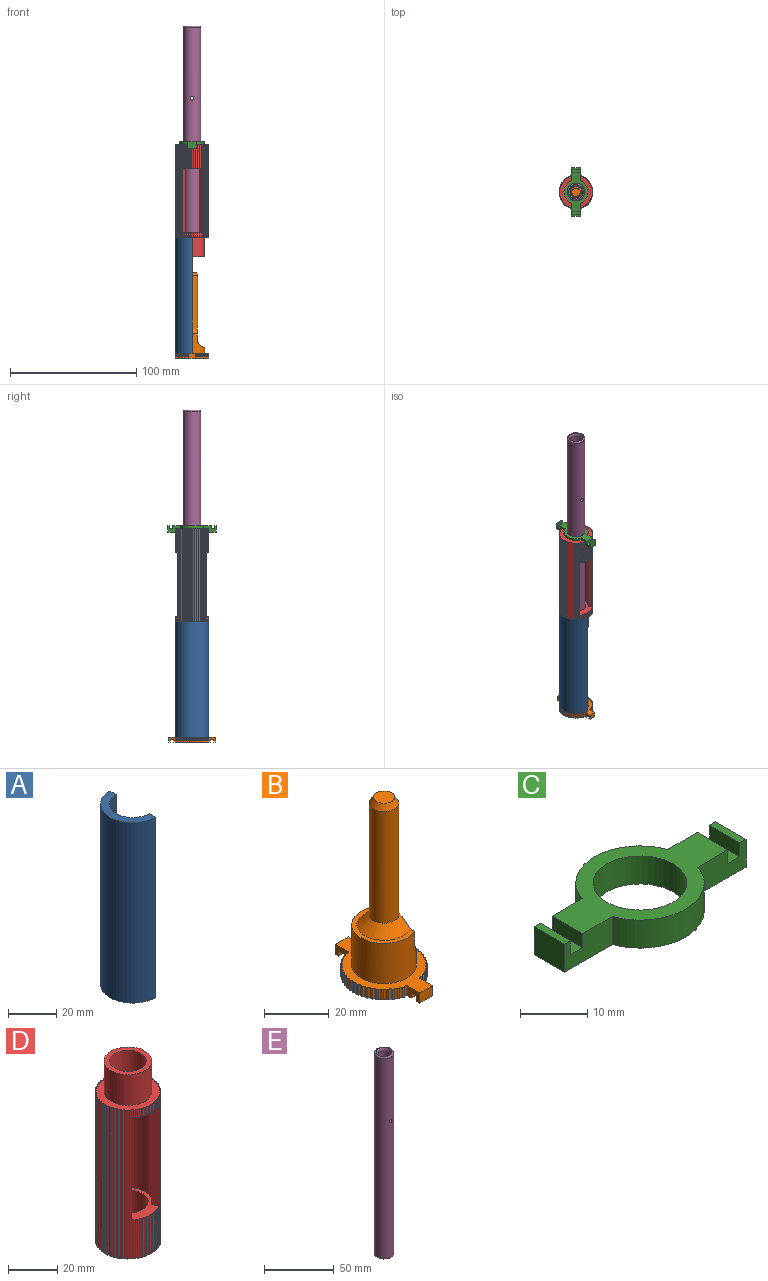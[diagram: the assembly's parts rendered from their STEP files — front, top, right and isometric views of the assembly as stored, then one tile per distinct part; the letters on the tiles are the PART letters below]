
ASSEMBLY  parts=5 mates=4
PART A: 6 faces, bbox 13.3x26.7x91.4 mm
  f0: cylinder r=9.65mm len=91.44mm, axis (0,0,-1), area 2772.7mm2, adj f2,f3,f4,f5
  f1: cylinder r=13.33mm len=91.44mm, axis (0,0,-1), area 3830.7mm2, adj f2,f3,f4,f5
  f2: plane 26.67x13.34mm, normal (0,0,1), area 133mm2, adj f0,f1,f4,f5
  f3: plane 26.67x13.34mm, normal (0,0,-1), area 133mm2, adj f0,f1,f4,f5
  f4: plane 91.44x3.68mm, normal (1,0,0), area 336.8mm2, adj f0,f1,f2,f3
  f5: plane 91.44x3.68mm, normal (1,0,0), area 336.8mm2, adj f0,f1,f2,f3
PART B: 110 faces, bbox 26.7x36.8x67.3 mm
  f0: plane 29.21x26.67mm, normal (0,0,-1), area 559.8mm2, adj f2,f3,f5,f6,f7,f8,f9,f10
  f1: plane 5.51x1.27mm, normal (0,0,-1), area 7mm2, adj f2,f99,f100,f106
  f2: plane 5.37x3.81mm, normal (1,0,0), area 15.6mm2, adj f0,f1,f49,f86,f100,f106,f107,f108
  f3: plane 5.37x3.81mm, normal (1,0,0), area 15.6mm2, adj f0,f4,f49,f54,f102,f103,f104,f105
  f4: plane 5.51x1.27mm, normal (0,0,-1), area 7mm2, adj f3,f101,f102,f104
  f5: cylinder r=13.33mm len=3.81mm, axis (0,0,-1), area 2mm2, adj f0,f49,f64,f96
  f6: cylinder r=13.33mm len=3.81mm, axis (0,0,-1), area 2mm2, adj f0,f49,f95,f96
  f7: cylinder r=13.33mm len=3.81mm, axis (0,0,-1), area 2mm2, adj f0,f49,f94,f95
  f8: cylinder r=13.33mm len=3.81mm, axis (0,0,-1), area 2mm2, adj f0,f49,f93,f94
  f9: cylinder r=13.33mm len=3.81mm, axis (0,0,-1), area 2mm2, adj f0,f49,f91,f92
  f10: cylinder r=13.33mm len=3.81mm, axis (0,0,-1), area 2mm2, adj f0,f49,f90,f91
  f11: cylinder r=13.33mm len=3.81mm, axis (0,0,-1), area 2mm2, adj f0,f49,f89,f90
  f12: cylinder r=13.33mm len=3.81mm, axis (0,0,-1), area 2mm2, adj f0,f49,f89,f93
  f13: cylinder r=13.33mm len=3.81mm, axis (0,0,-1), area 2mm2, adj f0,f49,f88,f92
  f14: cylinder r=13.33mm len=3.81mm, axis (0,0,-1), area 2mm2, adj f0,f49,f87,f88
  f15: cylinder r=13.33mm len=3.81mm, axis (0,0,-1), area 2mm2, adj f0,f49,f86,f87
  f16: cylinder r=13.33mm len=3.81mm, axis (0,0,-1), area 2mm2, adj f0,f49,f84,f85
  f17: cylinder r=13.33mm len=3.81mm, axis (0,0,-1), area 2mm2, adj f0,f49,f83,f84
  f18: cylinder r=13.33mm len=3.81mm, axis (0,0,-1), area 2mm2, adj f0,f49,f82,f83
  f19: cylinder r=13.33mm len=3.81mm, axis (0,0,-1), area 2mm2, adj f0,f49,f81,f82
  f20: cylinder r=13.33mm len=3.81mm, axis (0,0,-1), area 2mm2, adj f0,f49,f80,f81
  f21: cylinder r=13.33mm len=3.81mm, axis (0,0,-1), area 2mm2, adj f0,f49,f79,f80
  f22: cylinder r=13.33mm len=3.81mm, axis (0,0,-1), area 2mm2, adj f0,f49,f78,f79
  f23: cylinder r=13.33mm len=3.81mm, axis (0,0,-1), area 2mm2, adj f0,f49,f77,f78
  f24: cylinder r=13.33mm len=3.81mm, axis (0,0,-1), area 2mm2, adj f0,f49,f76,f77
  f25: cylinder r=13.33mm len=3.81mm, axis (0,0,-1), area 2mm2, adj f0,f49,f75,f76
  f26: cylinder r=13.33mm len=3.81mm, axis (0,0,-1), area 2mm2, adj f0,f49,f74,f75
  f27: cylinder r=13.33mm len=3.81mm, axis (0,0,-1), area 2mm2, adj f0,f49,f73,f74
  f28: cylinder r=13.33mm len=3.81mm, axis (0,0,-1), area 2mm2, adj f0,f49,f71,f72
  f29: cylinder r=13.33mm len=3.81mm, axis (0,0,-1), area 2mm2, adj f0,f49,f70,f71
  f30: cylinder r=13.33mm len=3.81mm, axis (0,0,-1), area 2mm2, adj f0,f49,f69,f70
  f31: cylinder r=13.33mm len=3.81mm, axis (0,0,-1), area 2mm2, adj f0,f49,f68,f69
  f32: cylinder r=13.33mm len=3.81mm, axis (0,0,-1), area 2mm2, adj f0,f49,f67,f68
  f33: cylinder r=13.33mm len=3.81mm, axis (0,0,-1), area 2mm2, adj f0,f49,f66,f67
  f34: cylinder r=13.33mm len=3.81mm, axis (0,0,-1), area 2mm2, adj f0,f49,f65,f66
  f35: cylinder r=13.33mm len=3.81mm, axis (0,0,-1), area 2mm2, adj f0,f49,f65,f73
  f36: cylinder r=13.33mm len=3.81mm, axis (0,0,-1), area 2mm2, adj f0,f49,f63,f64
  f37: cylinder r=13.33mm len=3.81mm, axis (0,0,-1), area 2mm2, adj f0,f49,f62,f63
  f38: cylinder r=13.33mm len=3.81mm, axis (0,0,-1), area 2mm2, adj f0,f49,f61,f62
  f39: cylinder r=13.33mm len=3.81mm, axis (0,0,-1), area 2mm2, adj f0,f49,f57,f61
  f40: cylinder r=13.33mm len=3.81mm, axis (0,0,-1), area 2mm2, adj f0,f49,f56,f60
  f41: cylinder r=13.33mm len=3.81mm, axis (0,0,-1), area 2mm2, adj f0,f49,f59,f60
  f42: cylinder r=13.33mm len=3.81mm, axis (0,0,-1), area 2mm2, adj f0,f49,f58,f59
  f43: cylinder r=13.33mm len=3.81mm, axis (0,0,-1), area 2mm2, adj f0,f49,f57,f58
  f44: cylinder r=13.33mm len=3.81mm, axis (0,0,-1), area 2mm2, adj f0,f49,f55,f56
  f45: cylinder r=13.33mm len=3.81mm, axis (0,0,-1), area 2mm2, adj f0,f49,f54,f55
  f46: cylinder r=10.02mm len=20.04mm, axis (0,0,-1), area 737.2mm2, adj f47,f49,f98
  f47: plane 20.04x14.18mm, normal (0,0,1), area 61.5mm2, adj f46,f97,f98
  f48: cylinder r=13.33mm len=3.81mm, axis (0,0,-1), area 2mm2, adj f0,f49,f53,f72
  f49: plane 36.83x26.67mm, normal (0,0,1), area 286.3mm2, adj f2,f3,f5,f6,f7,f8,f9,f10
  f50: cylinder r=4.57mm len=42.25mm, axis (0,0,-1), area 1205.6mm2, adj f52,f97,f98
  f51: plane 6.6x6.6mm, normal (0,0,1), area 34.3mm2, adj f52
  f52: cone r=3.3mm half-angle=30deg, axis (0,0,-1), area 62.8mm2, adj f50,f51
  f53: cylinder r=0.64mm len=3.81mm, axis (0,0,-1), area 5.5mm2, adj f0,f48,f49,f101
  f54: cylinder r=0.64mm len=3.81mm, axis (0,0,-1), area 5.5mm2, adj f0,f3,f45,f49
  f55: cylinder r=0.64mm len=3.81mm, axis (0,0,-1), area 5.5mm2, adj f0,f44,f45,f49
  f56: cylinder r=0.64mm len=3.81mm, axis (0,0,-1), area 5.5mm2, adj f0,f40,f44,f49
  f57: cylinder r=0.64mm len=3.81mm, axis (0,0,-1), area 5.5mm2, adj f0,f39,f43,f49
  f58: cylinder r=0.64mm len=3.81mm, axis (0,0,-1), area 5.5mm2, adj f0,f42,f43,f49
  f59: cylinder r=0.64mm len=3.81mm, axis (0,0,-1), area 5.5mm2, adj f0,f41,f42,f49
  f60: cylinder r=0.64mm len=3.81mm, axis (0,0,-1), area 5.5mm2, adj f0,f40,f41,f49
  f61: cylinder r=0.64mm len=3.81mm, axis (0,0,-1), area 5.5mm2, adj f0,f38,f39,f49
  f62: cylinder r=0.64mm len=3.81mm, axis (0,0,-1), area 5.5mm2, adj f0,f37,f38,f49
  f63: cylinder r=0.64mm len=3.81mm, axis (0,0,-1), area 5.5mm2, adj f0,f36,f37,f49
  f64: cylinder r=0.64mm len=3.81mm, axis (0,0,-1), area 5.5mm2, adj f0,f5,f36,f49
  f65: cylinder r=0.64mm len=3.81mm, axis (0,0,-1), area 5.5mm2, adj f0,f34,f35,f49
  f66: cylinder r=0.64mm len=3.81mm, axis (0,0,-1), area 5.5mm2, adj f0,f33,f34,f49
  f67: cylinder r=0.64mm len=3.81mm, axis (0,0,-1), area 5.5mm2, adj f0,f32,f33,f49
  f68: cylinder r=0.64mm len=3.81mm, axis (0,0,-1), area 5.5mm2, adj f0,f31,f32,f49
  f69: cylinder r=0.64mm len=3.81mm, axis (0,0,-1), area 5.5mm2, adj f0,f30,f31,f49
  f70: cylinder r=0.64mm len=3.81mm, axis (0,0,-1), area 5.5mm2, adj f0,f29,f30,f49
  f71: cylinder r=0.64mm len=3.81mm, axis (0,0,-1), area 5.5mm2, adj f0,f28,f29,f49
  f72: cylinder r=0.64mm len=3.81mm, axis (0,0,-1), area 5.5mm2, adj f0,f28,f48,f49
  f73: cylinder r=0.64mm len=3.81mm, axis (0,0,-1), area 5.5mm2, adj f0,f27,f35,f49
  f74: cylinder r=0.64mm len=3.81mm, axis (0,0,-1), area 5.5mm2, adj f0,f26,f27,f49
  f75: cylinder r=0.64mm len=3.81mm, axis (0,0,-1), area 5.5mm2, adj f0,f25,f26,f49
  f76: cylinder r=0.64mm len=3.81mm, axis (0,0,-1), area 5.5mm2, adj f0,f24,f25,f49
  f77: cylinder r=0.64mm len=3.81mm, axis (0,0,-1), area 5.5mm2, adj f0,f23,f24,f49
  f78: cylinder r=0.64mm len=3.81mm, axis (0,0,-1), area 5.5mm2, adj f0,f22,f23,f49
  f79: cylinder r=0.64mm len=3.81mm, axis (0,0,-1), area 5.5mm2, adj f0,f21,f22,f49
  f80: cylinder r=0.64mm len=3.81mm, axis (0,0,-1), area 5.5mm2, adj f0,f20,f21,f49
  f81: cylinder r=0.64mm len=3.81mm, axis (0,0,-1), area 5.5mm2, adj f0,f19,f20,f49
  f82: cylinder r=0.64mm len=3.81mm, axis (0,0,-1), area 5.5mm2, adj f0,f18,f19,f49
  f83: cylinder r=0.64mm len=3.81mm, axis (0,0,-1), area 5.5mm2, adj f0,f17,f18,f49
  f84: cylinder r=0.64mm len=3.81mm, axis (0,0,-1), area 5.5mm2, adj f0,f16,f17,f49
  f85: cylinder r=0.64mm len=3.81mm, axis (0,0,-1), area 5.5mm2, adj f0,f16,f49,f99
  f86: cylinder r=0.64mm len=3.81mm, axis (0,0,-1), area 5.5mm2, adj f0,f2,f15,f49
  f87: cylinder r=0.64mm len=3.81mm, axis (0,0,-1), area 5.5mm2, adj f0,f14,f15,f49
  f88: cylinder r=0.64mm len=3.81mm, axis (0,0,-1), area 5.5mm2, adj f0,f13,f14,f49
  f89: cylinder r=0.64mm len=3.81mm, axis (0,0,-1), area 5.5mm2, adj f0,f11,f12,f49
  f90: cylinder r=0.64mm len=3.81mm, axis (0,0,-1), area 5.5mm2, adj f0,f10,f11,f49
  f91: cylinder r=0.64mm len=3.81mm, axis (0,0,-1), area 5.5mm2, adj f0,f9,f10,f49
  f92: cylinder r=0.64mm len=3.81mm, axis (0,0,-1), area 5.5mm2, adj f0,f9,f13,f49
  f93: cylinder r=0.64mm len=3.81mm, axis (0,0,-1), area 5.5mm2, adj f0,f8,f12,f49
  f94: cylinder r=0.64mm len=3.81mm, axis (0,0,-1), area 5.5mm2, adj f0,f7,f8,f49
  f95: cylinder r=0.64mm len=3.81mm, axis (0,0,-1), area 5.5mm2, adj f0,f6,f7,f49
  f96: cylinder r=0.64mm len=3.81mm, axis (0,0,-1), area 5.5mm2, adj f0,f5,f6,f49
  f97: cone r=4.57mm half-angle=45deg, axis (0,0,-1), area 160.3mm2, adj f47,f50,f98
  f98: extruded ~18.29x18.11mm, area 262.4mm2, adj f46,f47,f50,f97
  f99: plane 5.37x3.81mm, normal (-1,0,0), area 15.6mm2, adj f0,f1,f49,f85,f100,f106,f107,f108
  f100: plane 5.51x3.81mm, normal (0,1,0), area 21mm2, adj f1,f2,f49,f99
  f101: plane 5.37x3.81mm, normal (-1,0,0), area 15.6mm2, adj f0,f4,f49,f53,f102,f103,f104,f105
  f102: plane 5.51x3.81mm, normal (0,-1,0), area 21mm2, adj f3,f4,f49,f101
  f103: plane 5.51x1.91mm, normal (0,-1,0), area 10.5mm2, adj f0,f3,f101,f105
  f104: plane 5.51x1.91mm, normal (0,1,0), area 10.5mm2, adj f3,f4,f101,f105
  f105: plane 5.51x2.54mm, normal (0,0,-1), area 14mm2, adj f3,f101,f103,f104
  f106: plane 5.51x1.91mm, normal (0,-1,0), area 10.5mm2, adj f1,f2,f99,f108
  f107: plane 5.51x1.91mm, normal (0,1,0), area 10.5mm2, adj f0,f2,f99,f108
  f108: plane 5.51x2.54mm, normal (0,0,-1), area 14mm2, adj f2,f99,f106,f107
  f109: torus R=8.33mm, axis (0,0,-1), area 391.7mm2
PART C: 19 faces, bbox 38.1x19.1x5.1 mm
  f0: plane 30.48x19.05mm, normal (0,0,1), area 208.3mm2, adj f2,f3,f4,f6,f7,f8,f10,f14
  f1: plane 6.35x1.27mm, normal (0,0,1), area 8.1mm2, adj f3,f5,f6,f17
  f2: plane 10.07x5.08mm, normal (0,-1,0), area 44.7mm2, adj f0,f4,f9,f11,f12,f13,f14,f15
  f3: plane 10.07x5.08mm, normal (0,-1,0), area 44.7mm2, adj f0,f1,f4,f5,f12,f16,f17,f18
  f4: cylinder r=9.53mm len=17.96mm, axis (0,0,-1), area 119.1mm2, adj f0,f2,f3,f12
  f5: plane 6.35x5.08mm, normal (1,0,0), area 32.3mm2, adj f1,f3,f6,f12
  f6: plane 10.07x5.08mm, normal (0,1,0), area 44.7mm2, adj f0,f1,f5,f7,f12,f16,f17,f18
  f7: cylinder r=9.53mm len=17.96mm, axis (0,0,-1), area 119.1mm2, adj f0,f6,f8,f12
  f8: plane 10.07x5.08mm, normal (0,1,0), area 44.7mm2, adj f0,f7,f9,f11,f12,f13,f14,f15
  f9: plane 6.35x5.08mm, normal (-1,0,0), area 32.3mm2, adj f2,f8,f11,f12
  f10: cylinder r=6.95mm len=13.89mm, axis (0,0,-1), area 221.7mm2, adj f0,f12
  f11: plane 6.35x1.27mm, normal (0,0,1), area 8.1mm2, adj f2,f8,f9,f13
  f12: plane 38.1x19.05mm, normal (0,0,-1), area 256.7mm2, adj f2,f3,f4,f5,f6,f7,f8,f9
  f13: plane 6.35x2.54mm, normal (1,0,0), area 16.1mm2, adj f2,f8,f11,f15
  f14: plane 6.35x2.54mm, normal (-1,0,0), area 16.1mm2, adj f0,f2,f8,f15
  f15: plane 6.35x2.54mm, normal (0,0,1), area 16.1mm2, adj f2,f8,f13,f14
  f16: plane 6.35x2.54mm, normal (1,0,0), area 16.1mm2, adj f0,f3,f6,f18
  f17: plane 6.35x2.54mm, normal (-1,0,0), area 16.1mm2, adj f1,f3,f6,f18
  f18: plane 6.35x2.54mm, normal (0,0,1), area 16.1mm2, adj f3,f6,f16,f17
PART D: 154 faces, bbox 26.7x26.7x88.9 mm
  f0: cylinder r=0.64mm len=19.05mm, axis (0,0,-1), area 27.4mm2, adj f1,f39,f144,f151
  f1: cylinder r=13.33mm len=19.05mm, axis (0,0,-1), area 10mm2, adj f0,f2,f144,f151
  f2: cylinder r=0.64mm len=19.05mm, axis (0,0,-1), area 27.4mm2, adj f1,f3,f144,f151
  f3: cylinder r=13.33mm len=19.05mm, axis (0,0,-1), area 10mm2, adj f2,f4,f144,f151
  f4: cylinder r=0.64mm len=19.05mm, axis (0,0,-1), area 27.4mm2, adj f3,f5,f144,f151
  f5: cylinder r=13.33mm len=19.05mm, axis (0,0,-1), area 10mm2, adj f4,f6,f144,f151
  f6: cylinder r=0.64mm len=19.05mm, axis (0,0,-1), area 27.4mm2, adj f5,f7,f144,f151
  f7: cylinder r=13.33mm len=19.05mm, axis (0,0,-1), area 10mm2, adj f6,f8,f144,f151
  f8: cylinder r=0.64mm len=19.05mm, axis (0,0,-1), area 27.4mm2, adj f7,f9,f144,f151
  f9: cylinder r=13.33mm len=19.05mm, axis (0,0,-1), area 10mm2, adj f8,f51,f144,f151
  f10: cylinder r=0.64mm len=19.05mm, axis (0,0,-1), area 27.4mm2, adj f11,f80,f144,f151
  f11: cylinder r=13.33mm len=19.05mm, axis (0,0,-1), area 10mm2, adj f10,f12,f144,f151
  f12: cylinder r=0.64mm len=19.05mm, axis (0,0,-1), area 27.4mm2, adj f11,f13,f144,f151
  f13: cylinder r=13.33mm len=19.05mm, axis (0,0,-1), area 10mm2, adj f12,f14,f144,f151
  f14: cylinder r=0.64mm len=19.05mm, axis (0,0,-1), area 27.4mm2, adj f13,f15,f144,f151
  f15: cylinder r=13.33mm len=19.05mm, axis (0,0,-1), area 10mm2, adj f14,f16,f144,f151
  f16: cylinder r=0.64mm len=19.05mm, axis (0,0,-1), area 27.4mm2, adj f15,f17,f144,f151
  f17: cylinder r=13.33mm len=19.05mm, axis (0,0,-1), area 10mm2, adj f16,f18,f144,f151
  f18: cylinder r=0.64mm len=19.05mm, axis (0,0,-1), area 27.4mm2, adj f17,f19,f144,f151
  f19: cylinder r=13.33mm len=19.05mm, axis (0,0,-1), area 10mm2, adj f18,f20,f144,f151
  f20: cylinder r=0.64mm len=19.05mm, axis (0,0,-1), area 27.4mm2, adj f19,f21,f144,f151
  f21: cylinder r=13.33mm len=19.05mm, axis (0,0,-1), area 10mm2, adj f20,f22,f144,f151
  f22: cylinder r=0.64mm len=19.05mm, axis (0,0,-1), area 27.4mm2, adj f21,f23,f144,f151
  f23: cylinder r=13.33mm len=19.05mm, axis (0,0,-1), area 10mm2, adj f22,f24,f144,f151
  f24: cylinder r=0.64mm len=19.05mm, axis (0,0,-1), area 27.4mm2, adj f23,f25,f144,f151
  f25: cylinder r=13.33mm len=19.05mm, axis (0,0,-1), area 10mm2, adj f24,f26,f144,f151
  f26: cylinder r=0.64mm len=19.05mm, axis (0,0,-1), area 27.4mm2, adj f25,f27,f144,f151
  f27: cylinder r=13.33mm len=19.05mm, axis (0,0,-1), area 10mm2, adj f26,f28,f144,f151
  f28: cylinder r=0.64mm len=19.05mm, axis (0,0,-1), area 27.4mm2, adj f27,f29,f144,f151
  f29: cylinder r=13.33mm len=19.05mm, axis (0,0,-1), area 10mm2, adj f28,f101,f144,f151
  f30: cylinder r=0.64mm len=19.05mm, axis (0,0,-1), area 27.4mm2, adj f31,f130,f144,f151
  f31: cylinder r=13.33mm len=19.05mm, axis (0,0,-1), area 10mm2, adj f30,f32,f144,f151
  f32: cylinder r=0.64mm len=19.05mm, axis (0,0,-1), area 27.4mm2, adj f31,f33,f144,f151
  f33: cylinder r=13.33mm len=19.05mm, axis (0,0,-1), area 10mm2, adj f32,f34,f144,f151
  f34: cylinder r=0.64mm len=19.05mm, axis (0,0,-1), area 27.4mm2, adj f33,f35,f144,f151
  f35: cylinder r=13.33mm len=19.05mm, axis (0,0,-1), area 10mm2, adj f34,f36,f144,f151
  f36: cylinder r=0.64mm len=19.05mm, axis (0,0,-1), area 27.4mm2, adj f35,f37,f144,f151
  f37: cylinder r=13.33mm len=19.05mm, axis (0,0,-1), area 10mm2, adj f36,f38,f144,f151
  f38: cylinder r=0.64mm len=19.05mm, axis (0,0,-1), area 27.4mm2, adj f37,f39,f144,f151
  f39: cylinder r=13.33mm len=19.05mm, axis (0,0,-1), area 10mm2, adj f0,f38,f144,f151
  f40: cylinder r=7.41mm len=19.05mm, axis (0,0,-1), area 886.7mm2, adj f143,f152
  f41: cylinder r=0.64mm len=3.81mm, axis (0,0,-1), area 5.5mm2, adj f42,f140,f141,f152
  f42: cylinder r=13.33mm len=3.81mm, axis (0,0,-1), area 2mm2, adj f41,f43,f141,f152
  f43: cylinder r=0.64mm len=3.81mm, axis (0,0,-1), area 5.5mm2, adj f42,f44,f141,f152
  f44: cylinder r=13.33mm len=3.81mm, axis (0,0,-1), area 2mm2, adj f43,f45,f141,f152
  f45: cylinder r=0.64mm len=3.81mm, axis (0,0,-1), area 5.5mm2, adj f44,f46,f141,f152
  f46: cylinder r=13.33mm len=3.81mm, axis (0,0,-1), area 2mm2, adj f45,f47,f141,f152
  f47: cylinder r=0.64mm len=3.81mm, axis (0,0,-1), area 5.5mm2, adj f46,f48,f141,f152
  f48: cylinder r=13.33mm len=3.81mm, axis (0,0,-1), area 2mm2, adj f47,f49,f141,f152
  f49: cylinder r=0.64mm len=3.81mm, axis (0,0,-1), area 5.5mm2, adj f48,f50,f141,f152
  f50: cylinder r=13.33mm len=3.81mm, axis (0,0,-1), area 2mm2, adj f49,f51,f141,f152
  f51: cylinder r=0.64mm len=73.66mm, axis (0,0,-1), area 106.1mm2, adj f9,f50,f52,f141,f144,f147
  f52: cylinder r=13.33mm len=73.66mm, axis (0,0,-1), area 38.7mm2, adj f51,f53,f141,f144
  f53: cylinder r=0.64mm len=73.66mm, axis (0,0,-1), area 106.1mm2, adj f52,f54,f141,f144
  f54: cylinder r=13.33mm len=73.66mm, axis (0,0,-1), area 38.7mm2, adj f53,f55,f141,f144
  f55: cylinder r=0.64mm len=73.66mm, axis (0,0,-1), area 106.1mm2, adj f54,f56,f141,f144
  f56: cylinder r=13.33mm len=73.66mm, axis (0,0,-1), area 38.7mm2, adj f55,f57,f141,f144
  f57: cylinder r=0.64mm len=73.66mm, axis (0,0,-1), area 106.1mm2, adj f56,f58,f141,f144
  f58: cylinder r=13.33mm len=73.66mm, axis (0,0,-1), area 38.7mm2, adj f57,f59,f141,f144
  f59: cylinder r=0.64mm len=73.66mm, axis (0,0,-1), area 106.1mm2, adj f58,f60,f141,f144
  f60: cylinder r=13.33mm len=73.66mm, axis (0,0,-1), area 38.7mm2, adj f59,f61,f141,f144
  f61: cylinder r=0.64mm len=73.66mm, axis (0,0,-1), area 106.1mm2, adj f60,f62,f141,f144
  f62: cylinder r=13.33mm len=73.66mm, axis (0,0,-1), area 38.7mm2, adj f61,f63,f141,f144
  f63: cylinder r=0.64mm len=73.66mm, axis (0,0,-1), area 106.1mm2, adj f62,f64,f141,f144
  f64: cylinder r=13.33mm len=73.66mm, axis (0,0,-1), area 38.7mm2, adj f63,f65,f141,f144
  f65: cylinder r=0.64mm len=73.66mm, axis (0,0,-1), area 106.1mm2, adj f64,f66,f141,f144
  f66: cylinder r=13.33mm len=73.66mm, axis (0,0,-1), area 38.7mm2, adj f65,f67,f141,f144
  f67: cylinder r=0.64mm len=73.66mm, axis (0,0,-1), area 106.1mm2, adj f66,f68,f141,f144
  f68: cylinder r=13.33mm len=73.66mm, axis (0,0,-1), area 38.7mm2, adj f67,f69,f141,f144
  f69: cylinder r=0.64mm len=73.66mm, axis (0,0,-1), area 106.1mm2, adj f68,f70,f141,f144
  f70: cylinder r=13.33mm len=73.66mm, axis (0,0,-1), area 38.7mm2, adj f69,f71,f141,f144
  f71: cylinder r=0.64mm len=73.66mm, axis (0,0,-1), area 106.1mm2, adj f70,f72,f141,f144
  f72: cylinder r=13.33mm len=73.66mm, axis (0,0,-1), area 38.7mm2, adj f71,f73,f141,f144
  f73: cylinder r=0.64mm len=73.66mm, axis (0,0,-1), area 106.1mm2, adj f72,f74,f141,f144
  f74: cylinder r=13.33mm len=73.66mm, axis (0,0,-1), area 38.7mm2, adj f73,f75,f141,f144
  f75: cylinder r=0.64mm len=73.66mm, axis (0,0,-1), area 106.1mm2, adj f74,f76,f141,f144
  f76: cylinder r=13.33mm len=73.66mm, axis (0,0,-1), area 38.7mm2, adj f75,f77,f141,f144
  f77: cylinder r=0.64mm len=73.66mm, axis (0,0,-1), area 106.1mm2, adj f76,f78,f141,f144
  f78: cylinder r=13.33mm len=73.66mm, axis (0,0,-1), area 38.7mm2, adj f77,f79,f141,f144
  f79: cylinder r=0.64mm len=73.66mm, axis (0,0,-1), area 106.1mm2, adj f78,f80,f141,f144
  f80: cylinder r=13.33mm len=73.66mm, axis (0,0,-1), area 38.7mm2, adj f10,f79,f81,f141,f144,f145
  f81: cylinder r=0.64mm len=3.81mm, axis (0,0,-1), area 5.5mm2, adj f80,f82,f141,f152
  f82: cylinder r=13.33mm len=3.81mm, axis (0,0,-1), area 2mm2, adj f81,f83,f141,f152
  f83: cylinder r=0.64mm len=3.81mm, axis (0,0,-1), area 5.5mm2, adj f82,f84,f141,f152
  f84: cylinder r=13.33mm len=3.81mm, axis (0,0,-1), area 2mm2, adj f83,f85,f141,f152
  f85: cylinder r=0.64mm len=3.81mm, axis (0,0,-1), area 5.5mm2, adj f84,f86,f141,f152
  f86: cylinder r=13.33mm len=3.81mm, axis (0,0,-1), area 2mm2, adj f85,f87,f141,f152
  f87: cylinder r=0.64mm len=3.81mm, axis (0,0,-1), area 5.5mm2, adj f86,f88,f141,f152
  f88: cylinder r=13.33mm len=3.81mm, axis (0,0,-1), area 2mm2, adj f87,f89,f141,f152
  f89: cylinder r=0.64mm len=3.81mm, axis (0,0,-1), area 5.5mm2, adj f88,f90,f141,f152
  f90: cylinder r=13.33mm len=3.81mm, axis (0,0,-1), area 2mm2, adj f89,f91,f141,f152
  f91: cylinder r=0.64mm len=3.81mm, axis (0,0,-1), area 5.5mm2, adj f90,f92,f141,f152
  f92: cylinder r=13.33mm len=3.81mm, axis (0,0,-1), area 2mm2, adj f91,f93,f141,f152
  f93: cylinder r=0.64mm len=3.81mm, axis (0,0,-1), area 5.5mm2, adj f92,f94,f141,f152
  f94: cylinder r=13.33mm len=3.81mm, axis (0,0,-1), area 2mm2, adj f93,f95,f141,f152
  f95: cylinder r=0.64mm len=3.81mm, axis (0,0,-1), area 5.5mm2, adj f94,f96,f141,f152
  f96: cylinder r=13.33mm len=3.81mm, axis (0,0,-1), area 2mm2, adj f95,f97,f141,f152
  f97: cylinder r=0.64mm len=3.81mm, axis (0,0,-1), area 5.5mm2, adj f96,f98,f141,f152
  f98: cylinder r=13.33mm len=3.81mm, axis (0,0,-1), area 2mm2, adj f97,f99,f141,f152
  f99: cylinder r=0.64mm len=3.81mm, axis (0,0,-1), area 5.5mm2, adj f98,f100,f141,f152
  f100: cylinder r=13.33mm len=3.81mm, axis (0,0,-1), area 2mm2, adj f99,f101,f141,f152
  f101: cylinder r=0.64mm len=73.66mm, axis (0,0,-1), area 106.1mm2, adj f29,f100,f102,f141,f144,f150
  f102: cylinder r=13.33mm len=73.66mm, axis (0,0,-1), area 38.7mm2, adj f101,f103,f141,f144
  f103: cylinder r=0.64mm len=73.66mm, axis (0,0,-1), area 106.1mm2, adj f102,f104,f141,f144
  f104: cylinder r=13.33mm len=73.66mm, axis (0,0,-1), area 38.7mm2, adj f103,f105,f141,f144
  f105: cylinder r=0.64mm len=73.66mm, axis (0,0,-1), area 106.1mm2, adj f104,f106,f141,f144
  f106: cylinder r=13.33mm len=73.66mm, axis (0,0,-1), area 38.7mm2, adj f105,f107,f141,f144
  f107: cylinder r=0.64mm len=73.66mm, axis (0,0,-1), area 106.1mm2, adj f106,f108,f141,f144
  f108: cylinder r=13.33mm len=73.66mm, axis (0,0,-1), area 38.7mm2, adj f107,f109,f141,f144
  f109: cylinder r=0.64mm len=73.66mm, axis (0,0,-1), area 106.1mm2, adj f108,f110,f141,f144
  f110: cylinder r=13.33mm len=73.66mm, axis (0,0,-1), area 38.7mm2, adj f109,f111,f141,f144
  f111: cylinder r=0.64mm len=73.66mm, axis (0,0,-1), area 106.1mm2, adj f110,f112,f141,f144
  f112: cylinder r=13.33mm len=73.66mm, axis (0,0,-1), area 38.7mm2, adj f111,f113,f141,f144
  f113: cylinder r=0.64mm len=73.66mm, axis (0,0,-1), area 106.1mm2, adj f112,f114,f141,f144
  f114: cylinder r=13.33mm len=73.66mm, axis (0,0,-1), area 38.7mm2, adj f113,f115,f141,f144
  f115: cylinder r=0.64mm len=73.66mm, axis (0,0,-1), area 106.1mm2, adj f114,f116,f141,f144
  f116: cylinder r=13.33mm len=73.66mm, axis (0,0,-1), area 38.7mm2, adj f115,f117,f141,f144
  f117: cylinder r=0.64mm len=73.66mm, axis (0,0,-1), area 106.1mm2, adj f116,f118,f141,f144
  f118: cylinder r=13.33mm len=73.66mm, axis (0,0,-1), area 38.7mm2, adj f117,f119,f141,f144
  f119: cylinder r=0.64mm len=73.66mm, axis (0,0,-1), area 106.1mm2, adj f118,f120,f141,f144
  f120: cylinder r=13.33mm len=73.66mm, axis (0,0,-1), area 38.7mm2, adj f119,f121,f141,f144
  f121: cylinder r=0.64mm len=73.66mm, axis (0,0,-1), area 106.1mm2, adj f120,f122,f141,f144
  f122: cylinder r=13.33mm len=73.66mm, axis (0,0,-1), area 38.7mm2, adj f121,f123,f141,f144
  f123: cylinder r=0.64mm len=73.66mm, axis (0,0,-1), area 106.1mm2, adj f122,f124,f141,f144
  f124: cylinder r=13.33mm len=73.66mm, axis (0,0,-1), area 38.7mm2, adj f123,f125,f141,f144
  f125: cylinder r=0.64mm len=73.66mm, axis (0,0,-1), area 106.1mm2, adj f124,f126,f141,f144
  f126: cylinder r=13.33mm len=73.66mm, axis (0,0,-1), area 38.7mm2, adj f125,f127,f141,f144
  f127: cylinder r=0.64mm len=73.66mm, axis (0,0,-1), area 106.1mm2, adj f126,f128,f141,f144
  f128: cylinder r=13.33mm len=73.66mm, axis (0,0,-1), area 38.7mm2, adj f127,f129,f141,f144
  f129: cylinder r=0.64mm len=73.66mm, axis (0,0,-1), area 106.1mm2, adj f128,f130,f141,f144
  f130: cylinder r=13.33mm len=73.66mm, axis (0,0,-1), area 38.7mm2, adj f30,f129,f131,f141,f144,f148
  f131: cylinder r=0.64mm len=3.81mm, axis (0,0,-1), area 5.5mm2, adj f130,f132,f141,f152
  f132: cylinder r=13.33mm len=3.81mm, axis (0,0,-1), area 2mm2, adj f131,f133,f141,f152
  f133: cylinder r=0.64mm len=3.81mm, axis (0,0,-1), area 5.5mm2, adj f132,f134,f141,f152
  f134: cylinder r=13.33mm len=3.81mm, axis (0,0,-1), area 2mm2, adj f133,f135,f141,f152
  f135: cylinder r=0.64mm len=3.81mm, axis (0,0,-1), area 5.5mm2, adj f134,f136,f141,f152
  f136: cylinder r=13.33mm len=3.81mm, axis (0,0,-1), area 2mm2, adj f135,f137,f141,f152
  f137: cylinder r=0.64mm len=3.81mm, axis (0,0,-1), area 5.5mm2, adj f136,f138,f141,f152
  f138: cylinder r=13.33mm len=3.81mm, axis (0,0,-1), area 2mm2, adj f137,f139,f141,f152
  f139: cylinder r=0.64mm len=3.81mm, axis (0,0,-1), area 5.5mm2, adj f138,f140,f141,f152
  f140: cylinder r=13.33mm len=3.81mm, axis (0,0,-1), area 2mm2, adj f41,f139,f141,f152
  f141: plane 26.67x26.66mm, normal (0,0,1), area 246mm2, adj f41,f42,f43,f44,f45,f46,f47,f48
  f142: cylinder r=9.72mm len=19.45mm, axis (0,0,-1), area 931.1mm2, adj f141,f143
  f143: plane 19.45x19.45mm, normal (0,0,1), area 124.6mm2, adj f40,f142
  f144: plane 26.67x26.66mm, normal (0,0,-1), area 334.2mm2, adj f0,f1,f2,f3,f4,f5,f6,f7
  f145: plane 50.8x2.74mm, normal (0.77,-0.64,0), area 180.6mm2, adj f80,f146,f151,f152
  f146: cylinder r=9.78mm len=50.8mm, axis (0,0,1), area 936.4mm2, adj f145,f147,f151,f152
  f147: plane 50.8x3mm, normal (0.84,0.54,0), area 180.6mm2, adj f51,f146,f151,f152
  f148: plane 50.8x2.74mm, normal (-0.77,0.64,0), area 180.6mm2, adj f130,f149,f151,f152
  f149: cylinder r=9.78mm len=50.8mm, axis (0,0,1), area 936.4mm2, adj f148,f150,f151,f152
  f150: plane 50.8x3mm, normal (-0.84,-0.54,0), area 180.6mm2, adj f101,f149,f151,f152
  f151: plane 26.66x19.56mm, normal (0,0,1), area 188.6mm2, adj f0,f1,f2,f3,f4,f5,f6,f7
  f152: plane 26.66x19.56mm, normal (0,0,-1), area 225.1mm2, adj f40,f41,f42,f43,f44,f45,f46,f47
  f153: cylinder r=8.15mm len=19.05mm, axis (0,0,-1), area 975.9mm2, adj f144,f151
PART E: 8 faces, bbox 15x15x178.2 mm
  f0: cylinder r=6.95mm len=175.35mm, axis (0,0,-1), area 7639.8mm2, adj f2,f3,f6,f7
  f1: cylinder r=4.83mm len=172.38mm, axis (0,0,-1), area 5214.9mm2, adj f4,f5,f6,f7
  f2: torus R=5.72mm, axis (0,0,-1), area 78.7mm2, adj f0,f5
  f3: torus R=5.72mm, axis (0,0,-1), area 28.7mm2, adj f0,f4
  f4: cone r=4.83mm half-angle=45deg, axis (0,0,-1), area 100.2mm2, adj f1,f3
  f5: torus R=9.91mm, axis (0,0,1), area 98.5mm2, adj f1,f2
  f6: cylinder r=1.39mm len=2.78mm, axis (0,-1,0), area 18.8mm2, adj f0,f1
  f7: cylinder r=1.39mm len=2.78mm, axis (0,-1,0), area 18.8mm2, adj f0,f1
PLACE A t=(-18.24,51.24,-10.38)mm
PLACE B t=(-18.24,51.24,-14.19)mm
PLACE C rot(axis=(0,0,-1),90deg) t=(-18.24,51.24,151.78)mm
PLACE D rot(axis=(0,1,0),180deg) t=(-16.55,43.93,84.87)mm
PLACE E t=(-18.24,51.24,50.18)mm
MATE fastened C.f10 <-> E.f0  axis (0,0,1) through (-18.24,51.24,156.86)mm
MATE revolute B.f46 <-> A.f0  axis (0,0,-1) through (-18.24,51.24,-10.38)mm
MATE slider E.f0 <-> A.f0  axis (0,0,-1) through (-18.24,51.24,159.4)mm
MATE revolute D.f1 <-> A.f0  axis (0,0,1) through (-18.24,51.24,81.06)mm
